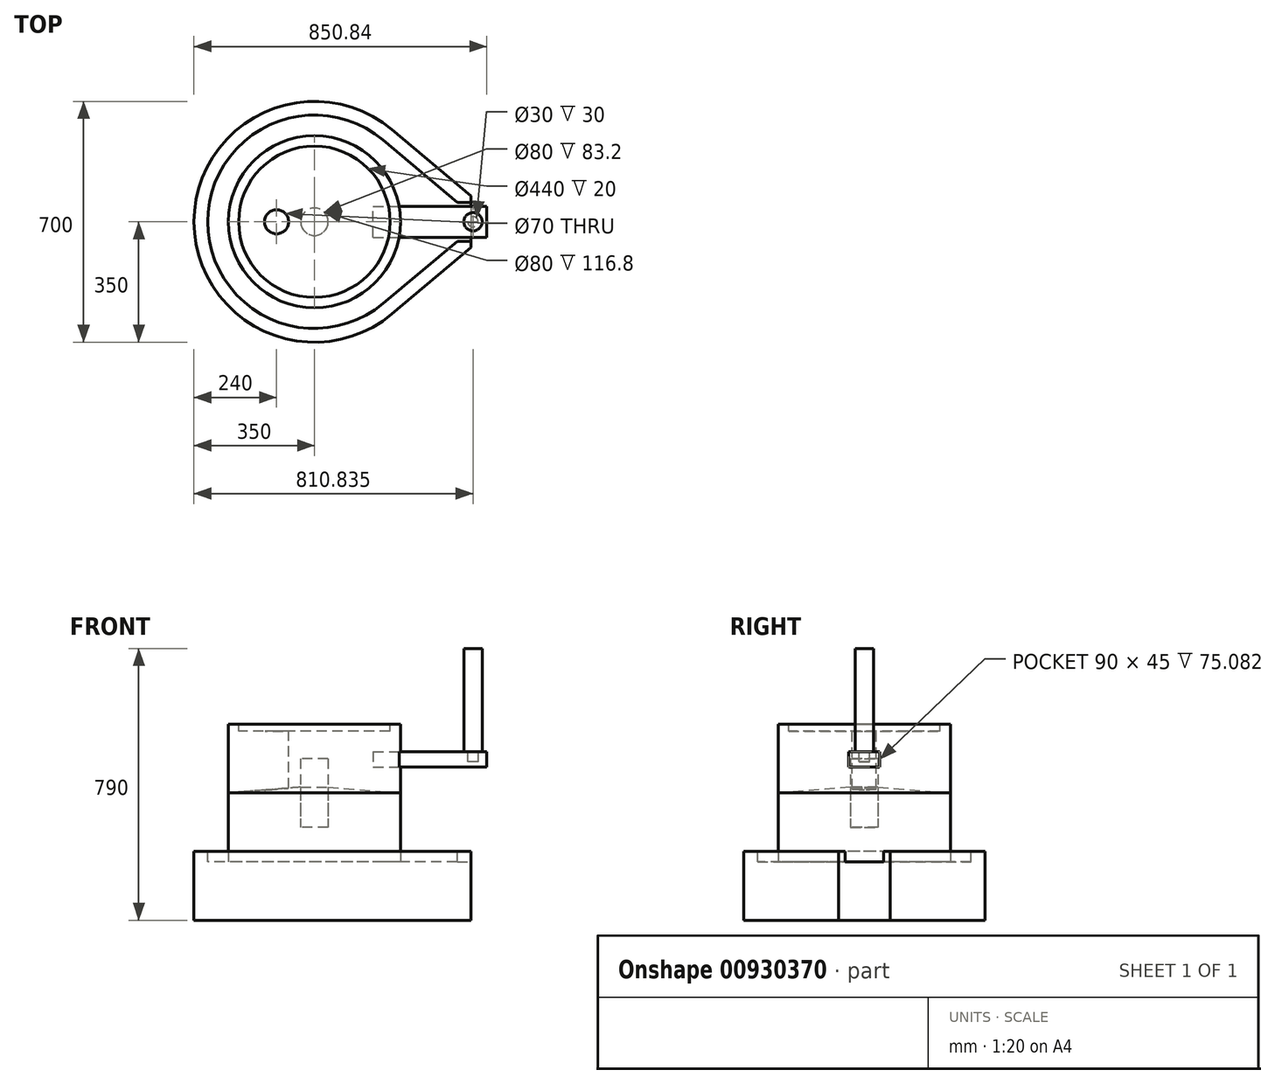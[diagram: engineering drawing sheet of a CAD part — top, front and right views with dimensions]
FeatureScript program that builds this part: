
annotation { "Feature Type Name" : "Feature", "Feature Type Description" : "" }
export const myFeature = defineFeature(function(context is Context, id is Id, definition is map)
    precondition{}
    {
        {
            var Q0;
            Q0=qCreatedBy(makeId("Top.planeOp"),FACE);
            var sketch = newSketch(context, id + "F0", { "sketchPlane" : qUnion([Q0])});
            skCircle(sketch, "E0", {"center": v(0, 0) * mm, "radius": 350 * mm});
            skLineSegment(sketch, "E1", {"start": v(454.84, 0) * mm, "end": v(454.84, 75) * mm});
            skLineSegment(sketch, "E2", {"start": v(454.84, 75) * mm, "end": v(225.14, 267.98) * mm});
            skLineSegment(sketch, "E3.MirrorCS", {"start": v(454.84, -75) * mm, "end": v(225.14, -267.98) * mm});
            skLineSegment(sketch, "E4.MirrorCS", {"start": v(454.84, 0) * mm, "end": v(454.84, -75) * mm});
            skSolve(sketch);
        }
        {
            var Q0;
            Q0 = qSketchRegion(id + "F0", true);
            extrude(context, id + "F1", {"entities" : qUnion([Q0]), "depth" : 200 * mm, "offsetDistance" : 25 * mm});
        }
        {
            var Q0;
            Q0=makeQuery(id+"F1.opExtrude","CAP_FACE",FACE,{"disambiguationData":[OSD([sQuery(id+"F0.wireOp",EDGE,"E0"),sQuery(id+"F0.wireOp",EDGE,"E1"),sQuery(id+"F0.wireOp",EDGE,"E2"),sQuery(id+"F0.wireOp",EDGE,"E3.MirrorCS"),sQuery(id+"F0.wireOp",EDGE,"E4.MirrorCS")])],"isStart":false});
            var sketch = newSketch(context, id + "F2", { "sketchPlane" : qUnion([Q0])});
            skArc(sketch, "E5.0", {"start": v(199.4, 237.35) * mm, "mid": v(-310, 0) * mm, "end": v(199.4, -237.35) * mm});
            skLineSegment(sketch, "E5.1", {"start": v(414.84, 56.36) * mm, "end": v(199.4, 237.35) * mm});
            skLineSegment(sketch, "E5.3", {"start": v(199.4, -237.35) * mm, "end": v(414.84, -56.36) * mm});
            skLineSegment(sketch, "E6", {"start": v(414.84, 56.36) * mm, "end": v(454.84, 56.36) * mm});
            skLineSegment(sketch, "E7", {"start": v(454.84, 56.36) * mm, "end": v(454.84, -56.36) * mm});
            skLineSegment(sketch, "E8", {"start": v(454.84, -56.36) * mm, "end": v(414.84, -56.36) * mm});
            skSolve(sketch);
        }
        {
            var Q0;
            Q0 = qSketchRegion(id + "F2", true);
            extrude(context, id + "F3", {"entities" : qUnion([Q0]), "operationType" : NewBodyOperationType.REMOVE, "oppositeDirection" : true, "depth" : 30 * mm, "offsetDistance" : 25 * mm});
        }
        {
            var Q0;
            Q0=makeQuery(id+"F3.boolean.opBoolean","COPY",FACE,{"derivedFrom":makeQuery(id+"F3.opExtrude","CAP_FACE",FACE,{"disambiguationData":[OSD([sQuery(id+"F2.wireOp",EDGE,"E5.0"),sQuery(id+"F2.wireOp",EDGE,"E5.1"),sQuery(id+"F2.wireOp",EDGE,"E5.3"),sQuery(id+"F2.wireOp",EDGE,"E6"),sQuery(id+"F2.wireOp",EDGE,"E7"),sQuery(id+"F2.wireOp",EDGE,"E8")])],"isStart":false})});
            var sketch = newSketch(context, id + "F4", { "sketchPlane" : qUnion([Q0])});
            skCircle(sketch, "E9", {"center": v(0, 0) * mm, "radius": 250 * mm});
            skSolve(sketch);
        }
        {
            var Q0;
            Q0 = qSketchRegion(id + "F4", true);
            extrude(context, id + "F5", {"entities" : qUnion([Q0]), "depth" : 200 * mm, "offsetDistance" : 25 * mm});
        }
        {
            var Q0;
            Q0=qCreatedBy(makeId("Front.planeOp"),FACE);
            var sketch = newSketch(context, id + "F6", { "sketchPlane" : qUnion([Q0])});
            skLineSegment(sketch, "E10", {"start": v(0, 390) * mm, "end": v(0, 370) * mm});
            skLineSegment(sketch, "E11", {"start": v(0, 370) * mm, "end": v(-250, 370) * mm});
            skLineSegment(sketch, "E12", {"start": v(-250, 370) * mm, "end": v(0, 390) * mm});
            skSolve(sketch);
        }
        {
            var Q0;
            Q0 = qSketchRegion(id + "F6", true);
            var Q1;
            Q1=sQuery(id+"F6.wireOp",EDGE,"E10");
            revolve(context, id + "F7", {"operationType" : NewBodyOperationType.ADD, "surfaceOperationType" : NewSurfaceOperationType.NEW, "entities" : qUnion([Q0]), "axis" : qUnion([Q1]), "revolveType" : RevolveType.FULL});
        }
        {
            var Q0;
            Q0=makeQuery(id+"F3.boolean.opBoolean","COPY",FACE,{"derivedFrom":makeQuery(id+"F3.opExtrude","CAP_FACE",FACE,{"disambiguationData":[OSD([sQuery(id+"F2.wireOp",EDGE,"E5.0"),sQuery(id+"F2.wireOp",EDGE,"E5.1"),sQuery(id+"F2.wireOp",EDGE,"E5.3"),sQuery(id+"F2.wireOp",EDGE,"E6"),sQuery(id+"F2.wireOp",EDGE,"E7"),sQuery(id+"F2.wireOp",EDGE,"E8")])],"isStart":false})});
            cPlane(context, id + "F8", {"entities" : qUnion([Q0]), "cplaneType" : CPlaneType.OFFSET, "offset" : 200 * mm, "width" : 150 * mm, "height" : 150 * mm});
        }
        {
            var Q0;
            Q0=qCreatedBy(id+"F8.planeOp",FACE);
            var sketch = newSketch(context, id + "F9", { "sketchPlane" : qUnion([Q0])});
            skCircle(sketch, "E13", {"center": v(0, 0) * mm, "radius": 40 * mm});
            skSolve(sketch);
        }
        {
            var Q0;
            Q0 = qSketchRegion(id + "F9", true);
            extrude(context, id + "F10", {"entities" : qUnion([Q0]), "endBound" : BoundingType.SYMMETRIC, "depth" : 200 * mm, "offsetDistance" : 25 * mm});
        }
        {
            var Q0;
            Q0=qCreatedBy(id+"F8.planeOp",FACE);
            var sketch = newSketch(context, id + "F11", { "sketchPlane" : qUnion([Q0])});
            skCircle(sketch, "E14.0", {"center": v(0, 0) * mm, "radius": 250 * mm});
            skSolve(sketch);
        }
        {
            var Q0;
            Q0=makeQuery(id+"F10.opExtrude","SWEPT_BODY",BODY,{"disambiguationData":[OSD([sQuery(id+"F9.wireOp",EDGE,"E13")])]});
            var Q1;
            Q1=makeQuery(id+"F5.opExtrude","SWEPT_BODY",BODY,{"disambiguationData":[OSD([sQuery(id+"F4.wireOp",EDGE,"E9")])]});
            booleanBodies(context, id + "F12", {"operationType" : BooleanOperationType.SUBTRACTION, "tools" : qUnion([Q0]), "targets" : qUnion([Q1]), "keepTools" : true});
        }
        {
            var Q0;
            Q0 = qSketchRegion(id + "F11", true);
            extrude(context, id + "F13", {"entities" : qUnion([Q0]), "depth" : 200 * mm, "offsetDistance" : 25 * mm});
        }
        {
            var Q0;
            Q0=makeQuery(id+"F10.opExtrude","SWEPT_BODY",BODY,{"disambiguationData":[OSD([sQuery(id+"F9.wireOp",EDGE,"E13")])]});
            var Q1;
            Q1=makeQuery(id+"F5.opExtrude","SWEPT_BODY",BODY,{"disambiguationData":[OSD([sQuery(id+"F4.wireOp",EDGE,"E9")])]});
            var Q2;
            Q2=makeQuery(id+"F13.opExtrude","SWEPT_BODY",BODY,{"disambiguationData":[OSD([sQuery(id+"F11.wireOp",EDGE,"E14.0")])]});
            booleanBodies(context, id + "F14", {"operationType" : BooleanOperationType.SUBTRACTION, "tools" : qUnion([Q0, Q1]), "targets" : qUnion([Q2]), "keepTools" : true});
        }
        {
            var Q0;
            Q0=makeQuery(id+"F13.opExtrude","CAP_FACE",FACE,{"disambiguationData":[OSD([sQuery(id+"F11.wireOp",EDGE,"E14.0")])],"isStart":false});
            var sketch = newSketch(context, id + "F15", { "sketchPlane" : qUnion([Q0])});
            skCircle(sketch, "E15.0", {"center": v(0, 0) * mm, "radius": 220 * mm});
            skSolve(sketch);
        }
        {
            var Q0;
            Q0 = qSketchRegion(id + "F15", true);
            extrude(context, id + "F16", {"entities" : qUnion([Q0]), "operationType" : NewBodyOperationType.REMOVE, "oppositeDirection" : true, "depth" : 20 * mm, "offsetDistance" : 25 * mm});
        }
        {
            var Q0;
            Q0=makeQuery(id+"F16.boolean.opBoolean","COPY",FACE,{"derivedFrom":makeQuery(id+"F16.opExtrude","CAP_FACE",FACE,{"disambiguationData":[OSD([sQuery(id+"F15.wireOp",EDGE,"E15.0")])],"isStart":false})});
            var sketch = newSketch(context, id + "F17", { "sketchPlane" : qUnion([Q0])});
            skCircle(sketch, "E16", {"center": v(-110, 0) * mm, "radius": 35 * mm});
            skSolve(sketch);
        }
        {
            var Q0;
            Q0 = qSketchRegion(id + "F17", true);
            var Q1;
            Q1=makeQuery(id+"F7.opRevolve","SWEPT_FACE",FACE,{"disambiguationData":[OSD([sQuery(id+"F6.wireOp",EDGE,"E12")])]});
            extrude(context, id + "F18", {"entities" : qUnion([Q0]), "operationType" : NewBodyOperationType.REMOVE, "endBound" : BoundingType.UP_TO_SURFACE, "oppositeDirection" : true, "depth" : 25 * mm, "endBoundEntityFace" : qUnion([Q1]), "offsetDistance" : 25 * mm});
        }
        {
            var Q0;
            Q0=makeQuery(id+"F1.opExtrude","SWEPT_FACE",FACE,{"disambiguationData":[OSD([sQuery(id+"F0.wireOp",EDGE,"E1"),sQuery(id+"F0.wireOp",EDGE,"E4.MirrorCS")])]});
            cPlane(context, id + "F19", {"entities" : qUnion([Q0]), "cplaneType" : CPlaneType.OFFSET, "offset" : 204 * mm, "oppositeDirection" : true, "width" : 150 * mm, "height" : 150 * mm});
        }
        {
            var Q0;
            Q0=qCreatedBy(id+"F19.planeOp",FACE);
            var sketch = newSketch(context, id + "F20", { "sketchPlane" : qUnion([Q0])});
            skLineSegment(sketch, "E17", {"start": v(-45, 490) * mm, "end": v(0, 490) * mm});
            skLineSegment(sketch, "E18", {"start": v(-45, 490) * mm, "end": v(-45, 445) * mm});
            skLineSegment(sketch, "E19", {"start": v(-45, 445) * mm, "end": v(0, 445) * mm});
            skLineSegment(sketch, "E20.MirrorCS", {"start": v(45, 490) * mm, "end": v(0, 490) * mm});
            skLineSegment(sketch, "E21.MirrorCS", {"start": v(45, 490) * mm, "end": v(45, 445) * mm});
            skLineSegment(sketch, "E22.MirrorCS", {"start": v(45, 445) * mm, "end": v(0, 445) * mm});
            skSolve(sketch);
        }
        {
            var Q0;
            Q0 = qSketchRegion(id + "F20", true);
            extrude(context, id + "F21", {"entities" : qUnion([Q0]), "oppositeDirection" : true, "depth" : 80 * mm, "offsetDistance" : 25 * mm});
        }
        {
            var Q0;
            Q0=makeQuery(id+"F21.opExtrude","CAP_FACE",FACE,{"disambiguationData":[OSD([sQuery(id+"F20.wireOp",EDGE,"E17"),sQuery(id+"F20.wireOp",EDGE,"E18"),sQuery(id+"F20.wireOp",EDGE,"E19"),sQuery(id+"F20.wireOp",EDGE,"E20.MirrorCS"),sQuery(id+"F20.wireOp",EDGE,"E21.MirrorCS"),sQuery(id+"F20.wireOp",EDGE,"E22.MirrorCS")])],"isStart":true});
            var sketch = newSketch(context, id + "F22", { "sketchPlane" : qUnion([Q0])});
            skLineSegment(sketch, "E23.bottom", {"start": v(-45, 490) * mm, "end": v(45, 490) * mm});
            skLineSegment(sketch, "E23.top", {"start": v(-45, 445) * mm, "end": v(45, 445) * mm});
            skLineSegment(sketch, "E23.left", {"start": v(-45, 490) * mm, "end": v(-45, 445) * mm});
            skLineSegment(sketch, "E23.right", {"start": v(45, 490) * mm, "end": v(45, 445) * mm});
            skSolve(sketch);
        }
        {
            var Q0;
            Q0 = qSketchRegion(id + "F22", true);
            extrude(context, id + "F23", {"entities" : qUnion([Q0]), "operationType" : NewBodyOperationType.ADD, "depth" : 250 * mm, "offsetDistance" : 25 * mm});
        }
        {
            var Q0;
            Q0=makeQuery(id+"F23.boolean.opBoolean","MERGE",FACE,{"derivedFrom":[makeQuery(id+"F21.opExtrude","SWEPT_FACE",FACE,{"disambiguationData":[OSD([sQuery(id+"F20.wireOp",EDGE,"E17"),sQuery(id+"F20.wireOp",EDGE,"E20.MirrorCS")])]}),makeQuery(id+"F23.opExtrude","SWEPT_FACE",FACE,{"disambiguationData":[OSD([sQuery(id+"F22.wireOp",EDGE,"E23.bottom")])]})]});
            var sketch = newSketch(context, id + "F24", { "sketchPlane" : qUnion([Q0])});
            skCircle(sketch, "E24", {"center": v(460.84, 0) * mm, "radius": 15 * mm});
            skSolve(sketch);
        }
        {
            var Q0;
            Q0 = qSketchRegion(id + "F24", true);
            extrude(context, id + "F25", {"entities" : qUnion([Q0]), "oppositeDirection" : true, "depth" : 30 * mm, "offsetDistance" : 25 * mm});
        }
        {
            var Q0;
            Q0=makeQuery(id+"F25.opExtrude","SWEPT_BODY",BODY,{"disambiguationData":[OSD([sQuery(id+"F24.wireOp",EDGE,"E24")])]});
            var Q1;
            Q1=makeQuery(id+"F21.opExtrude","SWEPT_BODY",BODY,{"disambiguationData":[OSD([sQuery(id+"F20.wireOp",EDGE,"E17"),sQuery(id+"F20.wireOp",EDGE,"E18"),sQuery(id+"F20.wireOp",EDGE,"E19"),sQuery(id+"F20.wireOp",EDGE,"E20.MirrorCS"),sQuery(id+"F20.wireOp",EDGE,"E21.MirrorCS"),sQuery(id+"F20.wireOp",EDGE,"E22.MirrorCS")])]});
            booleanBodies(context, id + "F26", {"operationType" : BooleanOperationType.SUBTRACTION, "tools" : qUnion([Q0]), "targets" : qUnion([Q1]), "keepTools" : true});
        }
        {
            var Q0;
            Q0=makeQuery(id+"F25.opExtrude","CAP_FACE",FACE,{"disambiguationData":[OSD([sQuery(id+"F24.wireOp",EDGE,"E24")])],"isStart":true});
            var sketch = newSketch(context, id + "F27", { "sketchPlane" : qUnion([Q0])});
            skCircle(sketch, "E25", {"center": v(460.84, 0) * mm, "radius": 26.57 * mm});
            skSolve(sketch);
        }
        {
            var Q0;
            Q0 = qSketchRegion(id + "F27", true);
            extrude(context, id + "F28", {"entities" : qUnion([Q0]), "depth" : 300 * mm, "offsetDistance" : 25 * mm});
        }
        {
            var Q0;
            Q0=makeQuery(id+"F21.opExtrude","SWEPT_BODY",BODY,{"disambiguationData":[OSD([sQuery(id+"F20.wireOp",EDGE,"E17"),sQuery(id+"F20.wireOp",EDGE,"E18"),sQuery(id+"F20.wireOp",EDGE,"E19"),sQuery(id+"F20.wireOp",EDGE,"E20.MirrorCS"),sQuery(id+"F20.wireOp",EDGE,"E21.MirrorCS"),sQuery(id+"F20.wireOp",EDGE,"E22.MirrorCS")])]});
            var Q1;
            Q1=makeQuery(id+"F13.opExtrude","SWEPT_BODY",BODY,{"disambiguationData":[OSD([sQuery(id+"F11.wireOp",EDGE,"E14.0")])]});
            booleanBodies(context, id + "F29", {"operationType" : BooleanOperationType.SUBTRACTION, "tools" : qUnion([Q0]), "targets" : qUnion([Q1]), "keepTools" : true});
        }
    });
